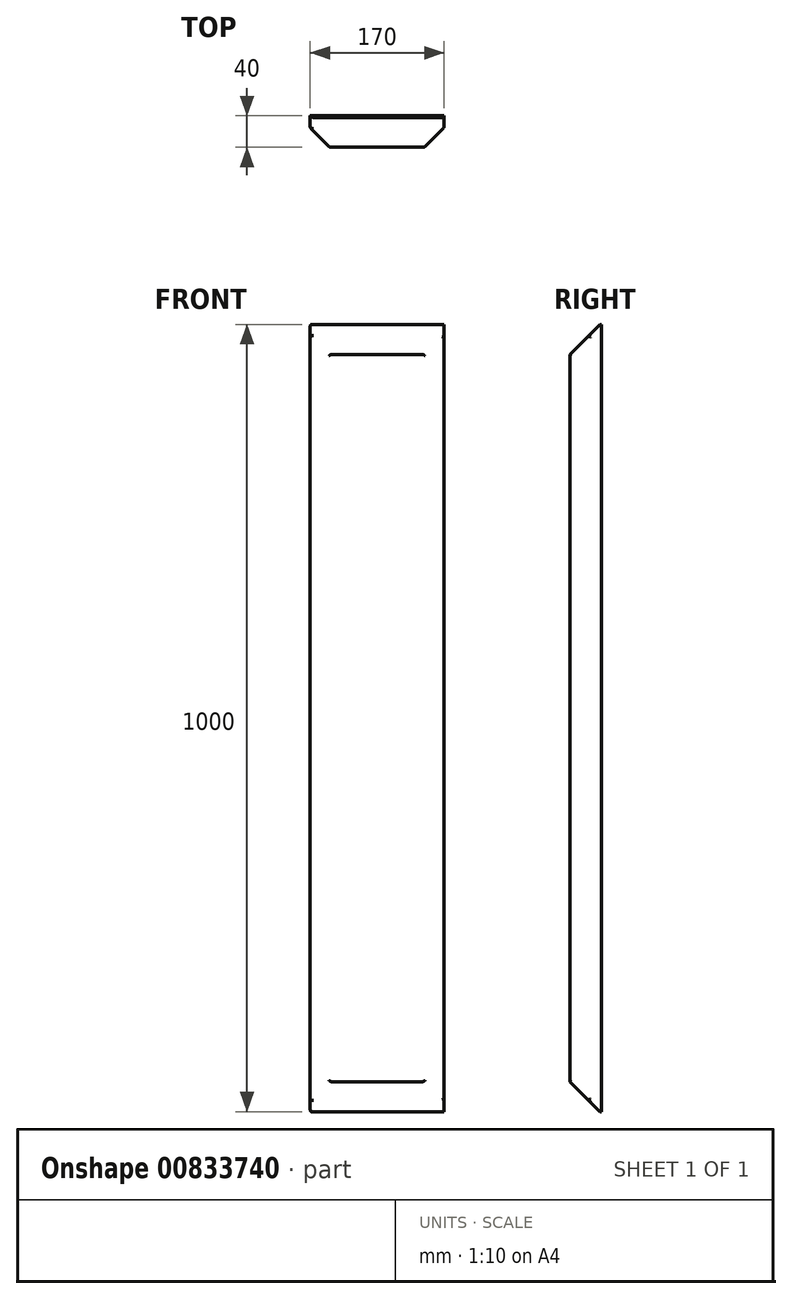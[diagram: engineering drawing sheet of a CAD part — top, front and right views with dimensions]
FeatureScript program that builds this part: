
annotation { "Feature Type Name" : "Feature", "Feature Type Description" : "" }
export const myFeature = defineFeature(function(context is Context, id is Id, definition is map)
    precondition{}
    {
        {
            var Q0;
            Q0=qCreatedBy(makeId("Top.planeOp"),FACE);
            var sketch = newSketch(context, id + "F0", { "sketchPlane" : qUnion([Q0])});
            skLineSegment(sketch, "E0.bottom", {"start": v(-85, 20) * mm, "end": v(85, 20) * mm});
            skLineSegment(sketch, "E0.top", {"start": v(-85, -20) * mm, "end": v(85, -20) * mm});
            skLineSegment(sketch, "E0.left", {"start": v(-85, 20) * mm, "end": v(-85, -20) * mm});
            skLineSegment(sketch, "E0.right", {"start": v(85, 20) * mm, "end": v(85, -20) * mm});
            skPoint(sketch, "E0.middle", {"position": v(0, 0) * mm});
            skSolve(sketch);
        }
        {
            var Q0;
            Q0=makeQuery(id+"F0.imprint","IMPRINT",FACE,{"disambiguationData":[TD([[makeQuery(id+"F0.imprint","IMPRINT",EDGE,{"derivedFrom":sQuery(id+"F0.wireOp",EDGE,"E0.bottom")}),-1.0]])]});
            extrude(context, id + "F1", {"entities" : qUnion([Q0]), "depth" : 1000 * mm, "offsetDistance" : 25 * mm});
        }
        {
            var Q0;
            Q0=makeQuery(id+"F1.opExtrude","SWEPT_FACE",FACE,{"disambiguationData":[OSD([sQuery(id+"F0.wireOp",EDGE,"E0.right")])]});
            var sketch = newSketch(context, id + "F2", { "sketchPlane" : qUnion([Q0])});
            skLineSegment(sketch, "E1", {"start": v(20, 0) * mm, "end": v(18, 0) * mm});
            skLineSegment(sketch, "E2", {"start": v(18, 0) * mm, "end": v(-20, 38) * mm});
            skLineSegment(sketch, "E3", {"start": v(-20, 38) * mm, "end": v(-20, 0) * mm});
            skLineSegment(sketch, "E4", {"start": v(-20, 0) * mm, "end": v(18, 0) * mm});
            skLineSegment(sketch, "E5", {"start": v(20, 1000) * mm, "end": v(18, 1000) * mm});
            skLineSegment(sketch, "E6", {"start": v(18, 1000) * mm, "end": v(-20, 962) * mm});
            skLineSegment(sketch, "E7", {"start": v(-20, 962) * mm, "end": v(-20, 1000) * mm});
            skLineSegment(sketch, "E8", {"start": v(-20, 1000) * mm, "end": v(18, 1000) * mm});
            skSolve(sketch);
        }
        {
            var Q0;
            Q0=makeQuery(id+"F2.imprint","IMPRINT",FACE,{"disambiguationData":[TD([[makeQuery(id+"F2.imprint","IMPRINT",EDGE,{"derivedFrom":sQuery(id+"F2.wireOp",EDGE,"E2")}),1.0]])]});
            var Q1;
            Q1=makeQuery(id+"F2.imprint","IMPRINT",FACE,{"disambiguationData":[TD([[makeQuery(id+"F2.imprint","IMPRINT",EDGE,{"derivedFrom":sQuery(id+"F2.wireOp",EDGE,"E6")}),-1.0]])]});
            extrude(context, id + "F3", {"entities" : qUnion([Q0, Q1]), "operationType" : NewBodyOperationType.REMOVE, "endBound" : BoundingType.THROUGH_ALL, "oppositeDirection" : true, "depth" : 25 * mm, "offsetDistance" : 25 * mm});
        }
        {
            var Q0;
            Q0=makeQuery(id+"F1.opExtrude","SWEPT_EDGE",EDGE,{"disambiguationData":[OSD([sQuery(id+"F0.wireOp",EDGE,"E0.top"),sQuery(id+"F0.wireOp",EDGE,"E0.right")])]});
            chamfer(context, id + "F4", {"entities" : qUnion([Q0]), "chamferType" : ChamferType.OFFSET_ANGLE, "width" : 25 * mm, "oppositeDirection" : false, "angle" : 45 * degree, "tangentPropagation" : true});
        }
        {
            var Q0;
            Q0=makeQuery(id+"F1.opExtrude","SWEPT_EDGE",EDGE,{"disambiguationData":[OSD([sQuery(id+"F0.wireOp",EDGE,"E0.top"),sQuery(id+"F0.wireOp",EDGE,"E0.left")])]});
            chamfer(context, id + "F5", {"entities" : qUnion([Q0]), "chamferType" : ChamferType.OFFSET_ANGLE, "width" : 25 * mm, "oppositeDirection" : true, "angle" : 45 * degree, "tangentPropagation" : true});
        }
        {
            var Q0;
            {var subQ0=sQuery(id+"F0.wireOp",EDGE,"E0.top");Q0=makeQuery(id+"F4.opChamfer","BLEND_EDGE",EDGE,{"blendedFrom":[makeQuery(id+"F1.opExtrude","SWEPT_EDGE",EDGE,{"disambiguationData":[OSD([subQ0,sQuery(id+"F0.wireOp",EDGE,"E0.right")])]}),makeQuery(id+"F1.opExtrude","SWEPT_FACE",FACE,{"disambiguationData":[OSD([subQ0])]})],"blendedInto":[makeQuery(id+"F1.opExtrude","SWEPT_FACE",FACE,{"disambiguationData":[OSD([subQ0])]})]});}
            var Q1;
            Q1=makeQuery(id+"F3.boolean.opBoolean","COPY",EDGE,{"derivedFrom":makeQuery(id+"F3.opExtrude","SWEPT_EDGE",EDGE,{"disambiguationData":[OSD([sQuery(id+"F0.wireOp",EDGE,"E0.top"),sQuery(id+"F0.wireOp",EDGE,"E0.right"),sQuery(id+"F2.wireOp",EDGE,"E2"),sQuery(id+"F2.wireOp",EDGE,"E3")])]})});
            var Q2;
            Q2=makeQuery(id+"F4.opChamfer","BLEND_EDGE",EDGE,{"blendedFrom":[makeQuery(id+"F1.opExtrude","SWEPT_EDGE",EDGE,{"disambiguationData":[OSD([sQuery(id+"F0.wireOp",EDGE,"E0.top"),sQuery(id+"F0.wireOp",EDGE,"E0.right")])]}),makeQuery(id+"F3.boolean.opBoolean","COPY",FACE,{"derivedFrom":makeQuery(id+"F3.opExtrude","SWEPT_FACE",FACE,{"disambiguationData":[OSD([sQuery(id+"F2.wireOp",EDGE,"E2")])]})})],"blendedInto":[makeQuery(id+"F3.boolean.opBoolean","COPY",FACE,{"derivedFrom":makeQuery(id+"F3.opExtrude","SWEPT_FACE",FACE,{"disambiguationData":[OSD([sQuery(id+"F2.wireOp",EDGE,"E2")])]})})]});
            var Q3;
            Q3=makeQuery(id+"F3.boolean.opBoolean","COPY",EDGE,{"derivedFrom":makeQuery(id+"F3.opExtrude","CAP_EDGE",EDGE,{"disambiguationData":[OSD([sQuery(id+"F2.wireOp",EDGE,"E2")])],"isStart":true})});
            var Q4;
            {var subQ0=sQuery(id+"F0.wireOp",EDGE,"E0.right");Q4=makeQuery(id+"F4.opChamfer","BLEND_EDGE",EDGE,{"blendedFrom":[makeQuery(id+"F1.opExtrude","SWEPT_EDGE",EDGE,{"disambiguationData":[OSD([sQuery(id+"F0.wireOp",EDGE,"E0.top"),subQ0])]}),makeQuery(id+"F1.opExtrude","SWEPT_FACE",FACE,{"disambiguationData":[OSD([subQ0])]})],"blendedInto":[makeQuery(id+"F1.opExtrude","SWEPT_FACE",FACE,{"disambiguationData":[OSD([subQ0])]})]});}
            var Q5;
            Q5=makeQuery(id+"F3.boolean.opBoolean","INTERSECT",EDGE,{"derivedFrom":[makeQuery(id+"F1.opExtrude","SWEPT_FACE",FACE,{"disambiguationData":[OSD([sQuery(id+"F0.wireOp",EDGE,"E0.left")])]}),makeQuery(id+"F3.opExtrude","SWEPT_FACE",FACE,{"disambiguationData":[OSD([sQuery(id+"F2.wireOp",EDGE,"E2")])]})]});
            var Q6;
            Q6=makeQuery(id+"F5.opChamfer","BLEND_EDGE",EDGE,{"blendedFrom":[makeQuery(id+"F1.opExtrude","SWEPT_EDGE",EDGE,{"disambiguationData":[OSD([sQuery(id+"F0.wireOp",EDGE,"E0.top"),sQuery(id+"F0.wireOp",EDGE,"E0.left")])]}),makeQuery(id+"F3.boolean.opBoolean","COPY",FACE,{"derivedFrom":makeQuery(id+"F3.opExtrude","SWEPT_FACE",FACE,{"disambiguationData":[OSD([sQuery(id+"F2.wireOp",EDGE,"E2")])]})})],"blendedInto":[makeQuery(id+"F3.boolean.opBoolean","COPY",FACE,{"derivedFrom":makeQuery(id+"F3.opExtrude","SWEPT_FACE",FACE,{"disambiguationData":[OSD([sQuery(id+"F2.wireOp",EDGE,"E2")])]})})]});
            var Q7;
            {var subQ0=sQuery(id+"F0.wireOp",EDGE,"E0.top");Q7=makeQuery(id+"F5.opChamfer","BLEND_EDGE",EDGE,{"blendedFrom":[makeQuery(id+"F1.opExtrude","SWEPT_EDGE",EDGE,{"disambiguationData":[OSD([subQ0,sQuery(id+"F0.wireOp",EDGE,"E0.left")])]}),makeQuery(id+"F1.opExtrude","SWEPT_FACE",FACE,{"disambiguationData":[OSD([subQ0])]})],"blendedInto":[makeQuery(id+"F1.opExtrude","SWEPT_FACE",FACE,{"disambiguationData":[OSD([subQ0])]})]});}
            var Q8;
            Q8=makeQuery(id+"F4.opChamfer","BLEND_EDGE",EDGE,{"blendedFrom":[makeQuery(id+"F1.opExtrude","SWEPT_EDGE",EDGE,{"disambiguationData":[OSD([sQuery(id+"F0.wireOp",EDGE,"E0.top"),sQuery(id+"F0.wireOp",EDGE,"E0.right")])]}),makeQuery(id+"F3.boolean.opBoolean","COPY",FACE,{"derivedFrom":makeQuery(id+"F3.opExtrude","SWEPT_FACE",FACE,{"disambiguationData":[OSD([sQuery(id+"F2.wireOp",EDGE,"E6")])]})})],"blendedInto":[makeQuery(id+"F3.boolean.opBoolean","COPY",FACE,{"derivedFrom":makeQuery(id+"F3.opExtrude","SWEPT_FACE",FACE,{"disambiguationData":[OSD([sQuery(id+"F2.wireOp",EDGE,"E6")])]})})]});
            var Q9;
            Q9=makeQuery(id+"F3.boolean.opBoolean","COPY",EDGE,{"derivedFrom":makeQuery(id+"F3.opExtrude","SWEPT_EDGE",EDGE,{"disambiguationData":[OSD([sQuery(id+"F0.wireOp",EDGE,"E0.top"),sQuery(id+"F0.wireOp",EDGE,"E0.right"),sQuery(id+"F2.wireOp",EDGE,"E6"),sQuery(id+"F2.wireOp",EDGE,"E7")])]})});
            var Q10;
            Q10=makeQuery(id+"F3.boolean.opBoolean","COPY",EDGE,{"derivedFrom":makeQuery(id+"F3.opExtrude","CAP_EDGE",EDGE,{"disambiguationData":[OSD([sQuery(id+"F2.wireOp",EDGE,"E6")])],"isStart":true})});
            var Q11;
            Q11=makeQuery(id+"F5.opChamfer","BLEND_EDGE",EDGE,{"blendedFrom":[makeQuery(id+"F1.opExtrude","SWEPT_EDGE",EDGE,{"disambiguationData":[OSD([sQuery(id+"F0.wireOp",EDGE,"E0.top"),sQuery(id+"F0.wireOp",EDGE,"E0.left")])]}),makeQuery(id+"F3.boolean.opBoolean","COPY",FACE,{"derivedFrom":makeQuery(id+"F3.opExtrude","SWEPT_FACE",FACE,{"disambiguationData":[OSD([sQuery(id+"F2.wireOp",EDGE,"E6")])]})})],"blendedInto":[makeQuery(id+"F3.boolean.opBoolean","COPY",FACE,{"derivedFrom":makeQuery(id+"F3.opExtrude","SWEPT_FACE",FACE,{"disambiguationData":[OSD([sQuery(id+"F2.wireOp",EDGE,"E6")])]})})]});
            var Q12;
            Q12=makeQuery(id+"F3.boolean.opBoolean","INTERSECT",EDGE,{"derivedFrom":[makeQuery(id+"F1.opExtrude","SWEPT_FACE",FACE,{"disambiguationData":[OSD([sQuery(id+"F0.wireOp",EDGE,"E0.left")])]}),makeQuery(id+"F3.opExtrude","SWEPT_FACE",FACE,{"disambiguationData":[OSD([sQuery(id+"F2.wireOp",EDGE,"E6")])]})]});
            var Q13;
            {var subQ0=sQuery(id+"F0.wireOp",EDGE,"E0.left");Q13=makeQuery(id+"F5.opChamfer","BLEND_EDGE",EDGE,{"blendedFrom":[makeQuery(id+"F1.opExtrude","SWEPT_EDGE",EDGE,{"disambiguationData":[OSD([sQuery(id+"F0.wireOp",EDGE,"E0.top"),subQ0])]}),makeQuery(id+"F1.opExtrude","SWEPT_FACE",FACE,{"disambiguationData":[OSD([subQ0])]})],"blendedInto":[makeQuery(id+"F1.opExtrude","SWEPT_FACE",FACE,{"disambiguationData":[OSD([subQ0])]})]});}
            fillet(context, id + "F6", {"entities" : qUnion([Q0, Q1, Q2, Q3, Q4, Q5, Q6, Q7, Q8, Q9, Q10, Q11, Q12, Q13]), "radius" : 4 * mm, "tangentPropagation" : true, "allowEdgeOverflow" : false});
        }
    });
